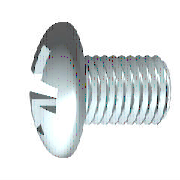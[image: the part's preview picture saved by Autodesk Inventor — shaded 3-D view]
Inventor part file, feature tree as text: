
AUTODESK INVENTOR PART (.ipt)
format: ipt  version: 2020 (Build 240168000, 168)  size: 279,552 bytes
history: native  units: mm (DEFAULTED — no unit token found)
features: other x2, plane x2, extrude x1
ambient origin geometry x7: Origin, YZ Plane, XZ Plane, X Axis, Y Axis, Z Axis, Center Point
bodies: Solid1 (feature_tree)
feature tree (5):
  other  "Базовый элемент"
  plane  "Work Plane1"
  extrude  "Паз"  Depth=2.0mm
  other  "Вырез"
  plane  "Work Plane3"
